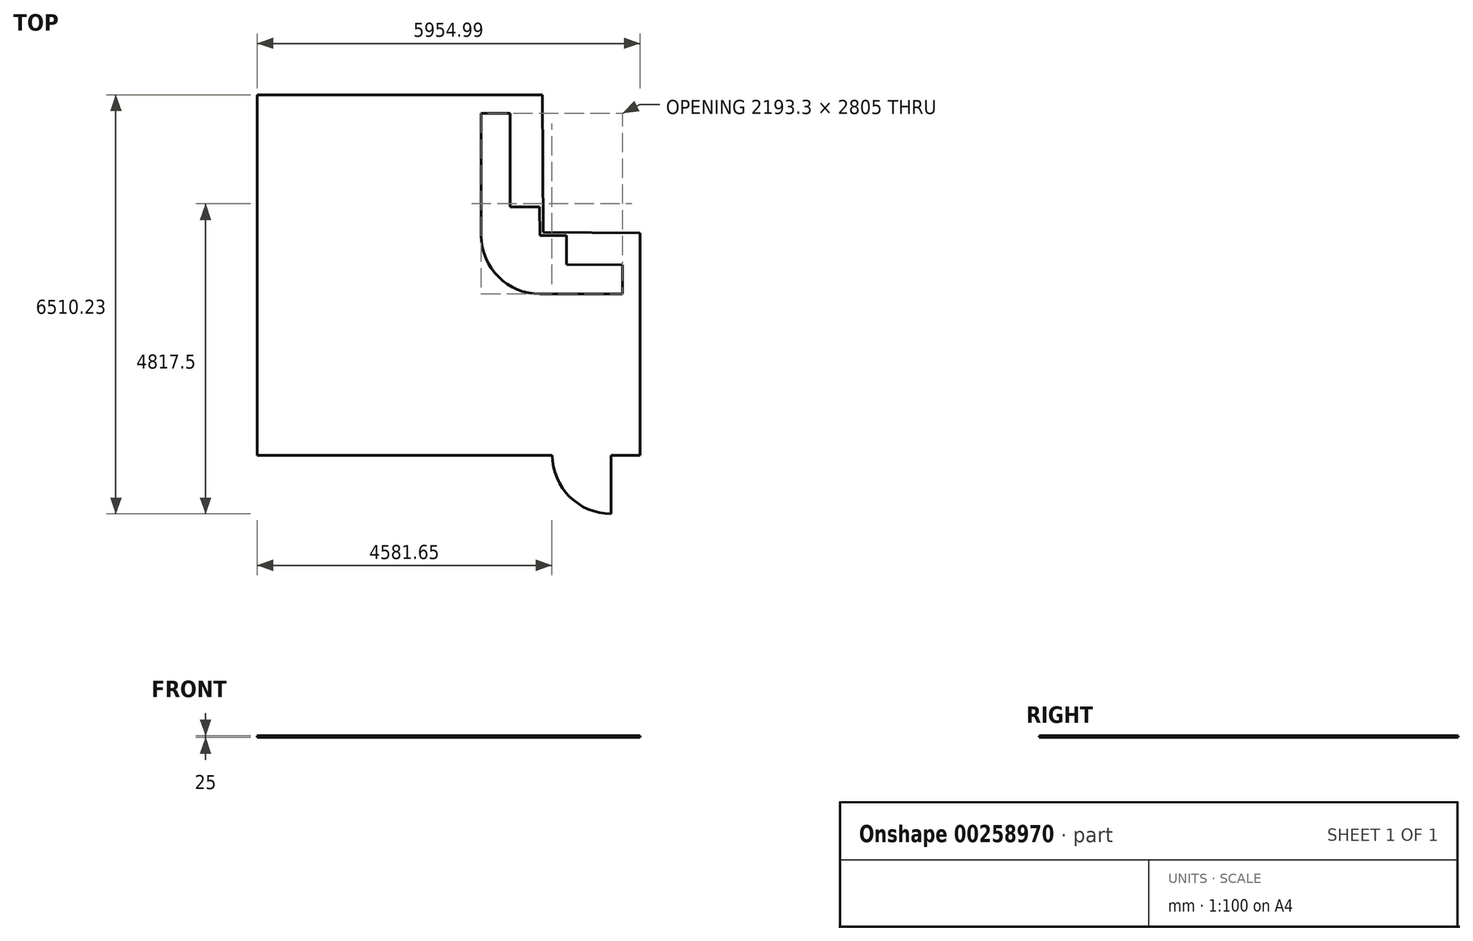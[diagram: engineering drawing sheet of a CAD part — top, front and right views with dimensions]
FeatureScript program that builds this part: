
annotation { "Feature Type Name" : "Feature", "Feature Type Description" : "" }
export const myFeature = defineFeature(function(context is Context, id is Id, definition is map)
    precondition{}
    {
        {
            var Q0;
            Q0=qCreatedBy(makeId("Top.planeOp"),FACE);
            var sketch = newSketch(context, id + "F0", { "sketchPlane" : qUnion([Q0])});
            skLineSegment(sketch, "E0", {"start": v(-1832, 2688.1) * mm, "end": v(-1832, -2911.9) * mm});
            skLineSegment(sketch, "E1", {"start": v(-1832, -2911.9) * mm, "end": v(2758, -2911.9) * mm});
            skLineSegment(sketch, "E2", {"start": v(-1832, 2688.1) * mm, "end": v(1653, 2688.1) * mm});
            skLineSegment(sketch, "E3", {"start": v(4122.98, -406.9) * mm, "end": v(4122.98, -2911.9) * mm});
            skLineSegment(sketch, "E4", {"start": v(1653, 498.1) * mm, "end": v(1653, 2688.1) * mm});
            skLineSegment(sketch, "E5", {"start": v(2562.98, -406.9) * mm, "end": v(4122.98, -406.9) * mm});
            skLineSegment(sketch, "E6", {"start": v(1653, 2688.1) * mm, "end": v(2553, 2688.1) * mm});
            skLineSegment(sketch, "E7", {"start": v(2103, 2688.1) * mm, "end": v(2103, 948.1) * mm});
            skLineSegment(sketch, "E8", {"start": v(2553, 2398.1) * mm, "end": v(1653, 2398.1) * mm});
            skLineSegment(sketch, "E9", {"start": v(2553, 2108.1) * mm, "end": v(1653, 2108.1) * mm});
            skLineSegment(sketch, "E10", {"start": v(1653, 1818.1) * mm, "end": v(2553, 1818.1) * mm});
            skLineSegment(sketch, "E11", {"start": v(1653, 1528.1) * mm, "end": v(2553, 1528.1) * mm});
            skLineSegment(sketch, "E12", {"start": v(1653, 1238.1) * mm, "end": v(2553, 1238.1) * mm});
            skLineSegment(sketch, "E13", {"start": v(2976.3, 503.16) * mm, "end": v(2976.3, -406.9) * mm});
            skLineSegment(sketch, "E14", {"start": v(4122.98, 493.1) * mm, "end": v(4122.98, -406.9) * mm});
            skLineSegment(sketch, "E15", {"start": v(3846.3, 493.1) * mm, "end": v(3846.3, -406.9) * mm});
            skLineSegment(sketch, "E16", {"start": v(3556.3, 493.1) * mm, "end": v(3556.3, -406.9) * mm});
            skLineSegment(sketch, "E17", {"start": v(3266.3, 493.1) * mm, "end": v(3266.3, -406.9) * mm});
            skPoint(sketch, "E18.startSnap0", {"position": v(4122.98, 43.1) * mm});
            skLineSegment(sketch, "E19", {"start": v(4122.98, 43.1) * mm, "end": v(2976.3, 48.14) * mm});
            skArc(sketch, "E20.filletArc", {"start": v(1180.16, -401.9) * mm, "mid": v(1181.63, -405.43) * mm, "end": v(1185.16, -406.9) * mm});
            skArc(sketch, "E21", {"start": v(1653, 498.1) * mm, "mid": v(1921.28, -142.12) * mm, "end": v(2562.98, -406.9) * mm});
            skLineSegment(sketch, "E22", {"start": v(2103, 948.1) * mm, "end": v(1653, 948.1) * mm});
            skLineSegment(sketch, "E23", {"start": v(2553, 2688.1) * mm, "end": v(2562.98, 503.1) * mm});
            skLineSegment(sketch, "E24", {"start": v(2103, 948.1) * mm, "end": v(2560.95, 948.1) * mm});
            skLineSegment(sketch, "E25", {"start": v(2562.98, 503.1) * mm, "end": v(4122.98, 493.1) * mm});
            skLineSegment(sketch, "E26", {"start": v(2976.3, 48.14) * mm, "end": v(2562.98, 48.14) * mm});
            skLineSegment(sketch, "E27", {"start": v(2103, 948.1) * mm, "end": v(2103, 503.1) * mm});
            skArc(sketch, "E28", {"start": v(2103, 503.1) * mm, "mid": v(2238.03, 179.62) * mm, "end": v(2562.98, 48.14) * mm});
            skLineSegment(sketch, "E29", {"start": v(2553, 2688.1) * mm, "end": v(2603, 2688.34) * mm});
            skLineSegment(sketch, "E30", {"start": v(4122.98, 493.1) * mm, "end": v(4122.98, 543.1) * mm});
            skLineSegment(sketch, "E31", {"start": v(4122.98, 543.1) * mm, "end": v(2612.75, 552.8) * mm});
            skLineSegment(sketch, "E32", {"start": v(2603, 2688.34) * mm, "end": v(2612.75, 552.8) * mm});
            skLineSegment(sketch, "E33", {"start": v(3668, -2911.9) * mm, "end": v(4122.98, -2911.9) * mm});
            skLineSegment(sketch, "E34", {"start": v(3668, -2911.9) * mm, "end": v(3668, -3821.9) * mm});
            skLineSegment(sketch, "E35", {"start": v(2758, -2911.9) * mm, "end": v(2758, -2911.9) * mm});
            skLineSegment(sketch, "E36", {"start": v(3668, -3821.9) * mm, "end": v(3668, -3821.9) * mm});
            skPoint(sketch, "E37.visualSharp", {"position": v(2758, -3821.9) * mm});
            skArc(sketch, "E37.filletArc", {"start": v(2758, -2911.9) * mm, "mid": v(3024.53, -3555.36) * mm, "end": v(3668, -3821.9) * mm});
            skSolve(sketch);
        }
        {
            var Q0;
            Q0 = qSketchRegion(id + "F0", true);
            extrude(context, id + "F1", {"entities" : qUnion([Q0]), "depth" : 25 * mm});
        }
    });
